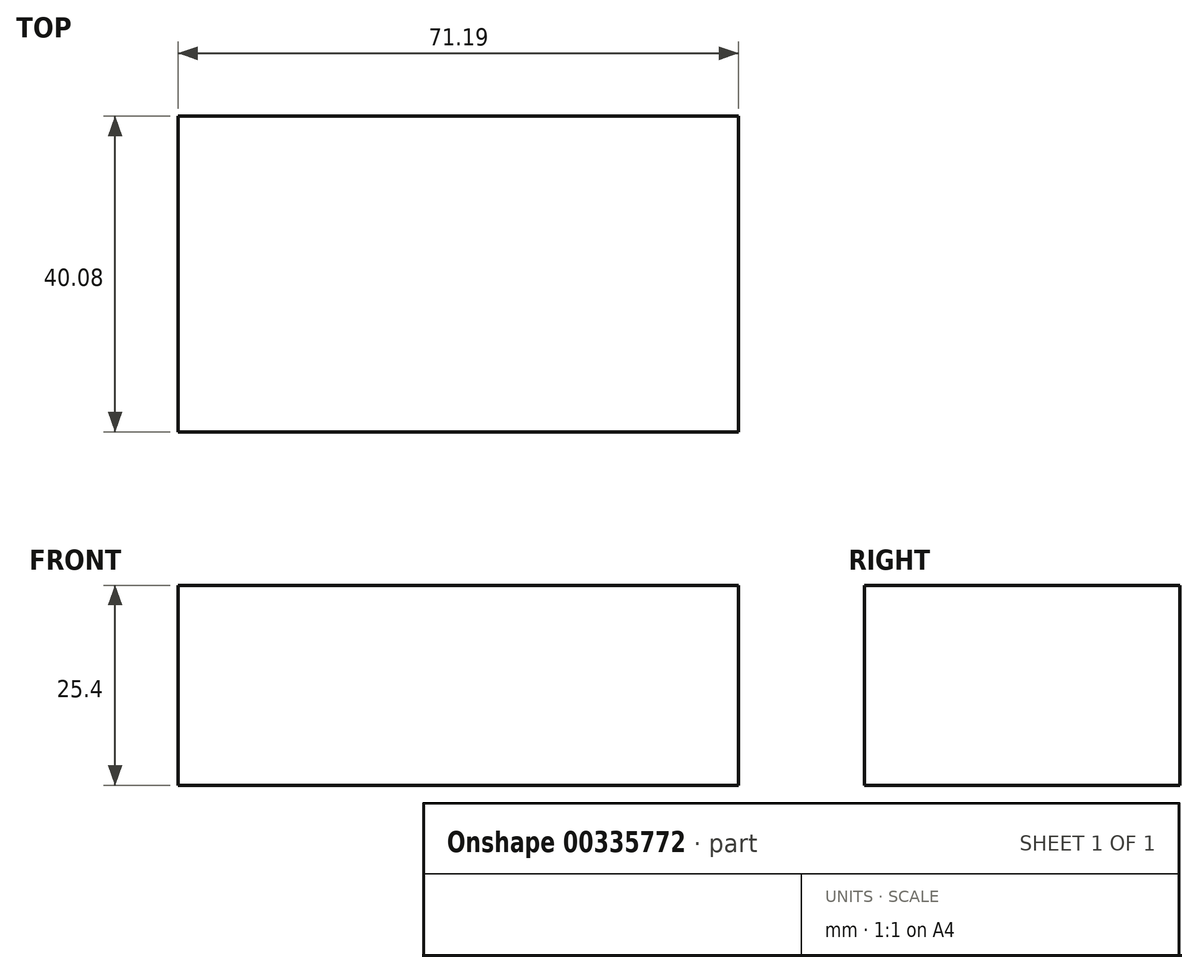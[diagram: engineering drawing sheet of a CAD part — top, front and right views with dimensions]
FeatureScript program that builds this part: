
annotation { "Feature Type Name" : "Feature", "Feature Type Description" : "" }
export const myFeature = defineFeature(function(context is Context, id is Id, definition is map)
    precondition{}
    {
        {
            var Q0;
            Q0=qCreatedBy(makeId("Top.planeOp"),FACE);
            var sketch = newSketch(context, id + "F0", { "sketchPlane" : qUnion([Q0])});
            skLineSegment(sketch, "E0.bottom", {"start": v(0, 0) * mm, "end": v(71.19, 0) * mm});
            skLineSegment(sketch, "E0.top", {"start": v(0, -40.08) * mm, "end": v(71.19, -40.08) * mm});
            skLineSegment(sketch, "E0.left", {"start": v(0, 0) * mm, "end": v(0, -40.08) * mm});
            skLineSegment(sketch, "E0.right", {"start": v(71.19, 0) * mm, "end": v(71.19, -40.08) * mm});
            skSolve(sketch);
        }
        {
            var Q0;
            Q0=makeQuery(id+"F0.imprint","IMPRINT",FACE,{"disambiguationData":[TD([[makeQuery(id+"F0.imprint","IMPRINT",EDGE,{"derivedFrom":sQuery(id+"F0.wireOp",EDGE,"E0.bottom")}),-1.0]])]});
            extrude(context, id + "F1", {"entities" : qUnion([Q0]), "depth" : 25.4 * mm});
        }
    });
